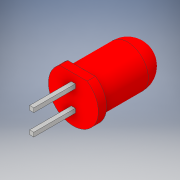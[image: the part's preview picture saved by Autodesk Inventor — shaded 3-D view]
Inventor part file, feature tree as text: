
AUTODESK INVENTOR PART (.ipt)
format: ipt  version: 2018 (Build 220112000, 112)  size: 150,016 bytes
history: native  units: mm
features: extrude x3, sketch x3, fillet x1
ambient origin geometry x8: Origin, YZ Plane, XZ Plane, XY Plane, X Axis, Y Axis, Z Axis, Center Point
bodies: Volumenkörper1 (feature_tree)
feature tree (7):
  extrude  "Höhe"  Depth=2.5mm TaperAngle=0.0deg
  fillet  "Radius_Kopf"  Radius=2.5mm
  extrude  "Kante"  Depth=1.0mm TaperAngle=0.0deg
  extrude  "Pin"  Depth=0.5mm
  sketch  "Skizze1"  dims[d0=5.0mm d1=8.0mm d2=0.0mm d3=2.5mm]
  sketch  "Skizze2"  dims[d4=6.0mm d5=1.0mm d6=0.0mm]
  sketch  "Skizze3"  dims[d7=2.54mm d8=0.5mm d9=0.5mm d10=5.0mm d11=0.0mm]
